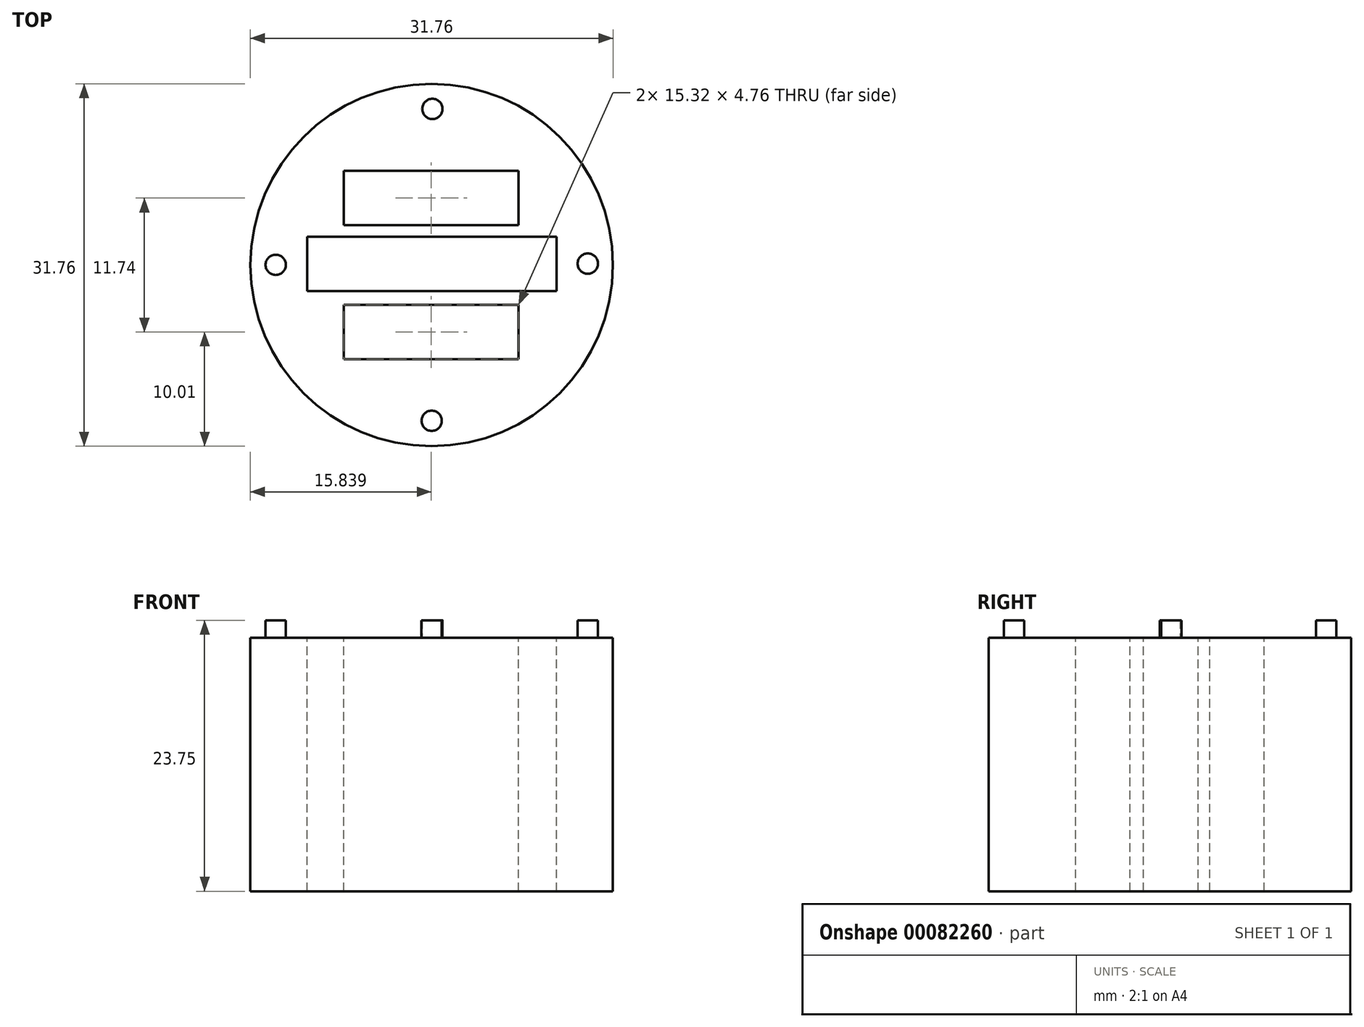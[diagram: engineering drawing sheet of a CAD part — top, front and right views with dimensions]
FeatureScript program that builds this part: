
annotation { "Feature Type Name" : "Feature", "Feature Type Description" : "" }
export const myFeature = defineFeature(function(context is Context, id is Id, definition is map)
    precondition{}
    {
        {
            var Q0;
            Q0=qCreatedBy(makeId("Top.planeOp"),FACE);
            var sketch = newSketch(context, id + "F0", { "sketchPlane" : qUnion([Q0])});
            skCircle(sketch, "E0", {"center": v(0, 0) * mm, "radius": 15.88 * mm});
            skSolve(sketch);
        }
        {
            var Q0;
            Q0=qSketchRegion(id+"F0",true);
            extrude(context, id + "F1", {"entities" : qUnion([Q0]), "depth" : 22.22 * mm});
        }
        {
            var Q0;
            Q0=makeQuery(id+"F1.opExtrude","CAP_FACE",FACE,{"disambiguationData":[OSD([sQuery(id+"F0.wireOp",EDGE,"E0")])],"isStart":true});
            var sketch = newSketch(context, id + "F2", { "sketchPlane" : qUnion([Q0])});
            skCircle(sketch, "E1", {"center": v(0, 0) * mm, "radius": 12.7 * mm});
            skSolve(sketch);
        }
        {
            var Q0;
            Q0=makeQuery(id+"F2.imprint","IMPRINT",FACE,{"disambiguationData":[TD([[makeQuery(id+"F2.imprint","IMPRINT",EDGE,{"derivedFrom":sQuery(id+"F2.wireOp",EDGE,"E1")}),-1.0]])]});
            var sketch = newSketch(context, id + "F3", { "sketchPlane" : qUnion([Q0])});
            skCircle(sketch, "E2", {"center": v(0, 13.65) * mm, "radius": 0.89 * mm});
            skCircle(sketch, "E3", {"center": v(-13.66, -0.02) * mm, "radius": 0.89 * mm});
            skCircle(sketch, "E4", {"center": v(0.06, -13.68) * mm, "radius": 0.89 * mm});
            skCircle(sketch, "E5", {"center": v(13.67, -0.12) * mm, "radius": 0.89 * mm});
            skSolve(sketch);
        }
        {
            var Q0;
            Q0=makeQuery(id+"F1.opExtrude","CAP_FACE",FACE,{"disambiguationData":[OSD([sQuery(id+"F0.wireOp",EDGE,"E0")])],"isStart":false});
            var sketch = newSketch(context, id + "F4", { "sketchPlane" : qUnion([Q0])});
            skCircle(sketch, "E6", {"center": v(0, 0) * mm, "radius": 11.35 * mm});
            skSolve(sketch);
        }
        {
            var Q0;
            Q0=qSketchRegion(id+"F3",true);
            extrude(context, id + "F5", {"entities" : qUnion([Q0]), "operationType" : NewBodyOperationType.ADD, "oppositeDirection" : true, "depth" : 23.75 * mm});
        }
        {
            var Q0;
            Q0=makeQuery(id+"F4.imprint","IMPRINT",FACE,{"disambiguationData":[TD([[makeQuery(id+"F4.imprint","IMPRINT",EDGE,{"derivedFrom":sQuery(id+"F4.wireOp",EDGE,"E6")}),-1.0]])]});
            var sketch = newSketch(context, id + "F7", { "sketchPlane" : qUnion([Q0])});
            skLineSegment(sketch, "E7.bottom", {"start": v(-10.9, 2.5) * mm, "end": v(10.93, 2.5) * mm});
            skLineSegment(sketch, "E7.top", {"start": v(-10.9, -2.3) * mm, "end": v(10.93, -2.3) * mm});
            skLineSegment(sketch, "E7.left", {"start": v(-10.9, 2.5) * mm, "end": v(-10.9, -2.3) * mm});
            skLineSegment(sketch, "E7.right", {"start": v(10.93, 2.5) * mm, "end": v(10.93, -2.3) * mm});
            skLineSegment(sketch, "E8.bottom", {"start": v(-7.7, 8.25) * mm, "end": v(7.62, 8.25) * mm});
            skLineSegment(sketch, "E8.top", {"start": v(-7.7, 3.49) * mm, "end": v(7.62, 3.49) * mm});
            skLineSegment(sketch, "E8.left", {"start": v(-7.7, 8.25) * mm, "end": v(-7.7, 3.49) * mm});
            skLineSegment(sketch, "E8.right", {"start": v(7.62, 8.25) * mm, "end": v(7.62, 3.49) * mm});
            skLineSegment(sketch, "E9.MirrorCS", {"start": v(7.62, -8.25) * mm, "end": v(7.62, -3.49) * mm});
            skLineSegment(sketch, "E10.MirrorCS", {"start": v(-7.7, -3.49) * mm, "end": v(7.62, -3.49) * mm});
            skLineSegment(sketch, "E11.MirrorCS", {"start": v(-7.7, -8.25) * mm, "end": v(7.62, -8.25) * mm});
            skLineSegment(sketch, "E12.MirrorCS", {"start": v(-7.7, -8.25) * mm, "end": v(-7.7, -3.49) * mm});
            skSolve(sketch);
        }
        {
            var Q0;
            Q0 = qSketchRegion(id + "F7", true);
            extrude(context, id + "F6", {"entities" : qUnion([Q0]), "operationType" : NewBodyOperationType.REMOVE, "oppositeDirection" : true, "depth" : 22.22 * mm});
        }
    });
